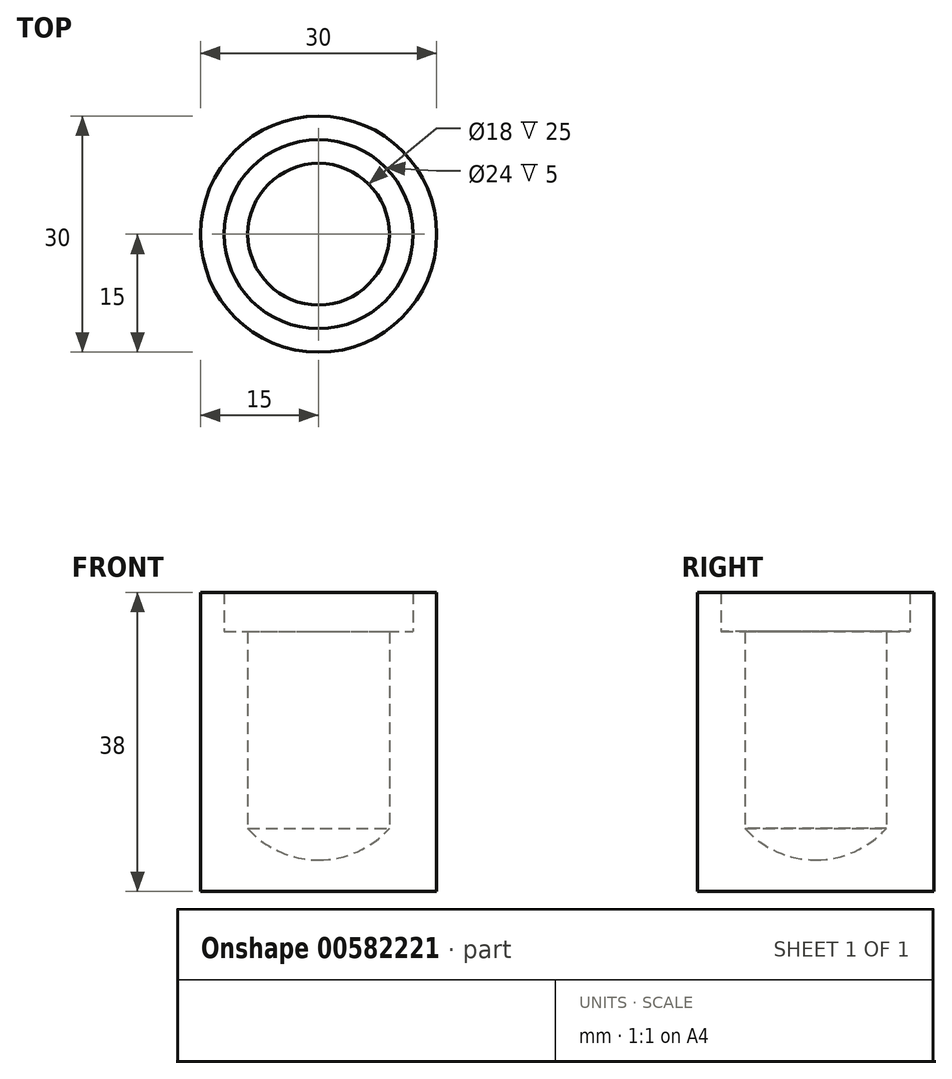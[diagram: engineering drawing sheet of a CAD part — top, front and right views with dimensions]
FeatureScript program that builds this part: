
annotation { "Feature Type Name" : "Feature", "Feature Type Description" : "" }
export const myFeature = defineFeature(function(context is Context, id is Id, definition is map)
    precondition{}
    {
        {
            var Q0;
            Q0=qCreatedBy(makeId("Front.planeOp"),FACE);
            var sketch = newSketch(context, id + "F0", { "sketchPlane" : qUnion([Q0])});
            skLineSegment(sketch, "E0.top", {"start": v(15, -4) * mm, "end": v(-15, -4) * mm});
            skLineSegment(sketch, "E0.left", {"start": v(15, 4) * mm, "end": v(15, -4) * mm});
            skLineSegment(sketch, "E0.right", {"start": v(-15, 4) * mm, "end": v(-15, -4) * mm});
            skPoint(sketch, "E0.middle", {"position": v(0, 0) * mm});
            skLineSegment(sketch, "E1.left", {"start": v(-15, 4) * mm, "end": v(-15, 29) * mm});
            skLineSegment(sketch, "E1.right", {"start": v(-9, 4) * mm, "end": v(-9, 29) * mm});
            skLineSegment(sketch, "E2.left", {"start": v(15, 4) * mm, "end": v(15, 29) * mm});
            skLineSegment(sketch, "E2.right", {"start": v(9, 4) * mm, "end": v(9, 29) * mm});
            skPoint(sketch, "E3.oppositeSnap0", {"position": v(12, 29) * mm});
            skLineSegment(sketch, "E3.top", {"start": v(15, 34) * mm, "end": v(12, 34) * mm});
            skLineSegment(sketch, "E3.left", {"start": v(15, 29) * mm, "end": v(15, 34) * mm});
            skLineSegment(sketch, "E3.right", {"start": v(12, 29) * mm, "end": v(12, 34) * mm});
            skLineSegment(sketch, "E4.top", {"start": v(-15, 34) * mm, "end": v(-12, 34) * mm});
            skLineSegment(sketch, "E4.left", {"start": v(-15, 29) * mm, "end": v(-15, 34) * mm});
            skLineSegment(sketch, "E4.right", {"start": v(-12, 29) * mm, "end": v(-12, 34) * mm});
            skArc(sketch, "E5", {"start": v(-9, 4) * mm, "mid": v(0, 0) * mm, "end": v(9, 4) * mm});
            skLineSegment(sketch, "E6", {"start": v(12, 29) * mm, "end": v(9, 29) * mm});
            skLineSegment(sketch, "E7", {"start": v(-12, 29) * mm, "end": v(-9, 29) * mm});
            skLineSegment(sketch, "E8", {"start": v(0, -4) * mm, "end": v(0, 0) * mm});
            skSolve(sketch);
        }
        {
            var Q0;
            {var subQ1=sQuery(id+"F0.wireOp",EDGE,"E0.right");Q0=makeQuery(id+"F0.imprint","IMPRINT",FACE,{"disambiguationData":[TD([[makeQuery(id+"F0.imprint","IMPRINT",EDGE,{"derivedFrom":subQ1}),1.0]])]});}
            var Q1;
            Q1=sQuery(id+"F0.wireOp",EDGE,"E8");
            revolve(context, id + "F1", {"entities" : qUnion([Q0]), "axis" : qUnion([Q1]), "revolveType" : RevolveType.FULL});
        }
    });
